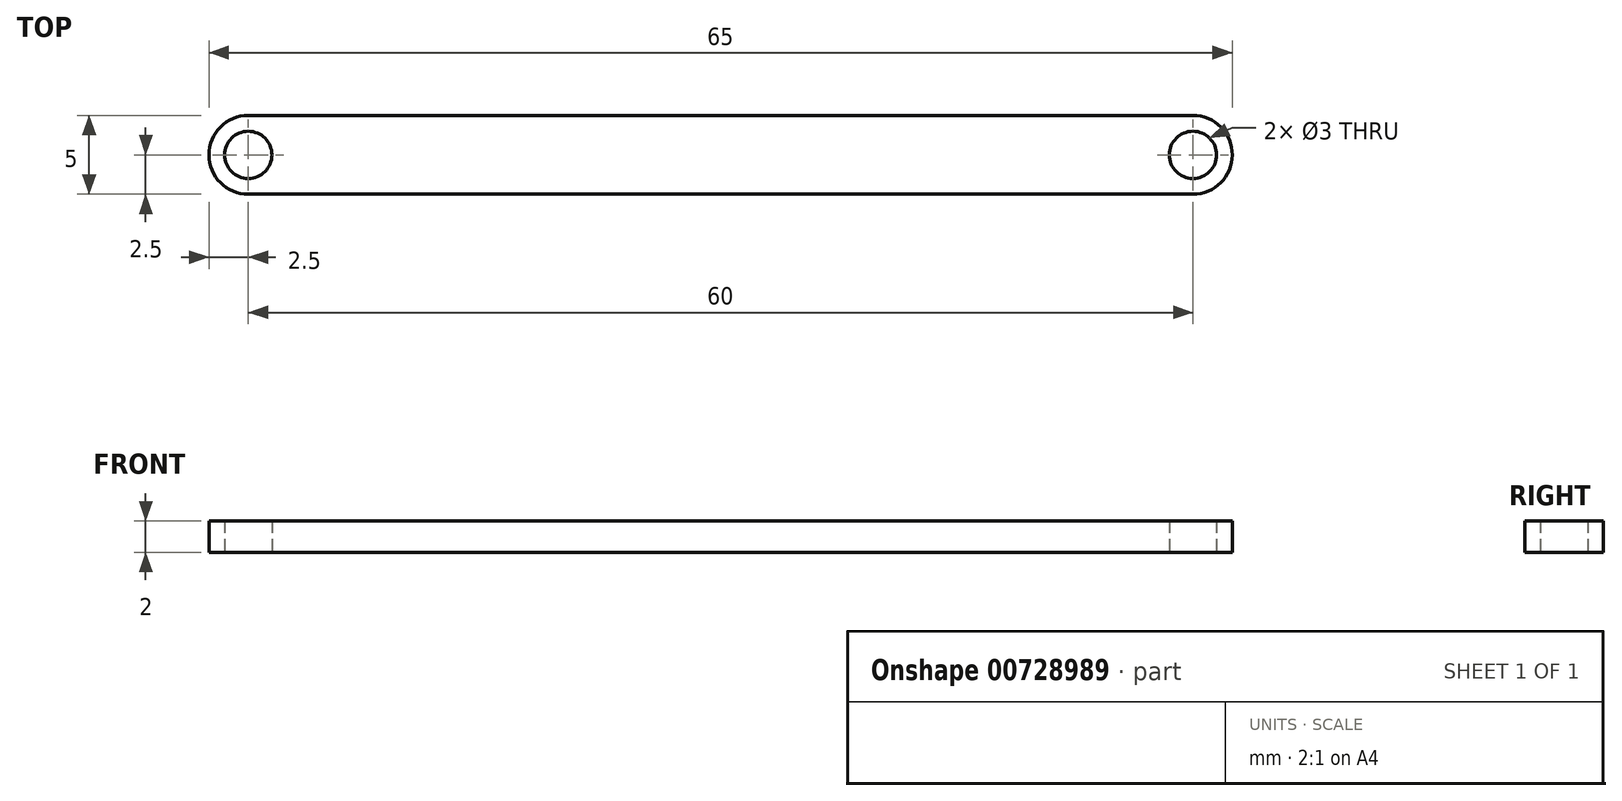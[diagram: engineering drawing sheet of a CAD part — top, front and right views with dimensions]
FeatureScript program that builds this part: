
annotation { "Feature Type Name" : "Feature", "Feature Type Description" : "" }
export const myFeature = defineFeature(function(context is Context, id is Id, definition is map)
    precondition{}
    {
        {
            var Q0;
            Q0=qCreatedBy(makeId("Top.planeOp"),FACE);
            var sketch = newSketch(context, id + "F0", { "sketchPlane" : qUnion([Q0])});
            skArc(sketch, "E0", {"start": v(-30, 2.5) * mm, "mid": v(-32.5, 0) * mm, "end": v(-30, -2.5) * mm});
            skArc(sketch, "E1", {"start": v(30, -2.5) * mm, "mid": v(32.5, 0) * mm, "end": v(30, 2.5) * mm});
            skLineSegment(sketch, "E2", {"start": v(-30, 2.5) * mm, "end": v(30, 2.5) * mm});
            skLineSegment(sketch, "E3", {"start": v(-30, -2.5) * mm, "end": v(30, -2.5) * mm});
            skCircle(sketch, "E4", {"center": v(-30, 0) * mm, "radius": 1.5 * mm});
            skCircle(sketch, "E5", {"center": v(30, 0) * mm, "radius": 1.5 * mm});
            skSolve(sketch);
        }
        {
            var Q0;
            Q0=makeQuery(id+"F0.imprint","IMPRINT",FACE,{"disambiguationData":[TD([[makeQuery(id+"F0.imprint","IMPRINT",EDGE,{"derivedFrom":sQuery(id+"F0.wireOp",EDGE,"E0")}),1.0]])]});
            extrude(context, id + "F1", {"entities" : qUnion([Q0]), "endBound" : BoundingType.SYMMETRIC, "depth" : 2 * mm, "offsetDistance" : 25 * mm});
        }
    });
